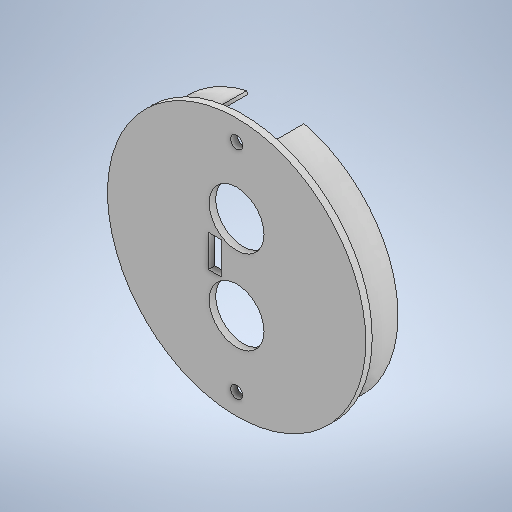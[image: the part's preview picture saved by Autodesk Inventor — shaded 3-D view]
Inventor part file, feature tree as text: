
AUTODESK INVENTOR PART (.ipt)
format: ipt  version: 2025.3 (Build 293356000, 356)  size: 276,992 bytes
history: native  units: in
note: dims shown in document units (in); Inventor stores cm internally (conversion verified against a paired STEP export)
features: reference x7, extrude x4, sketch x4, other x2, plane x1
ambient origin geometry x8: Origin, YZ Plane, XZ Plane, XY Plane, X Axis, Y Axis, Z Axis, Center Point
bodies: Solid1 (feature_tree)
feature tree (18):
  extrude  "Extrusion1"  Depth=0.0394in
  plane  "Work Plane1"
  extrude  "Extrusion2"  Depth=0.0787in TaperAngle=0.0deg
  extrude  "Extrusion3"  Depth=0.1476in
  extrude  "Extrusion4"  Depth=0.3937in
  sketch  "Sketch1"  dims[d0=0.0394in d1=0.0394in]
  reference  "Reference1"
  reference  "Reference2"
  sketch  "Sketch2"  dims[d2=0.3937in d3=0.0in d4=0.0787in d5=0.0in]
  reference  "Reference3"
  reference  "Reference4"
  reference  "Reference5"
  sketch  "Sketch3"  dims[d6=0.1476in d7=0.1476in]
  reference  "Reference6"
  reference  "Reference7"
  sketch  "Sketch4"  dims[d8=0.0787in d9=0.0in d10=0.7874in d11=1.7717in d12=0.6693in d13=0.6693in d14=1.0236in d15=0.5118in d16=0.1575in d17=0.3937in d18=0.3445in d19=0.3937in d20=0.0in]
  other  "Assembly1"
  other  "main_body:1"
